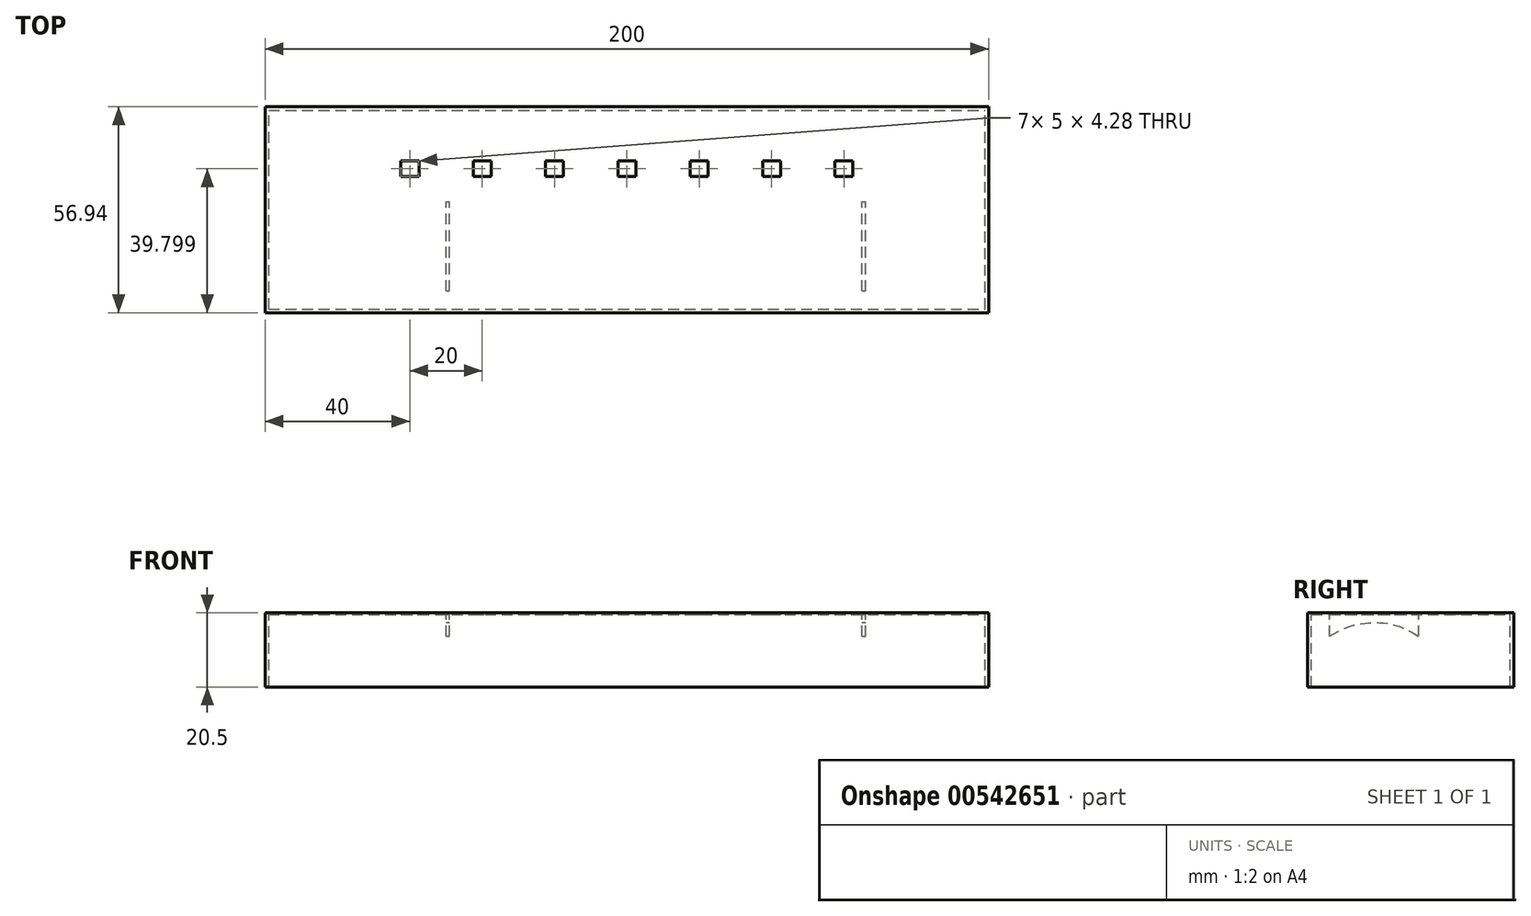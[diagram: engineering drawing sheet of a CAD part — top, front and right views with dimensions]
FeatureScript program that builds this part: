
annotation { "Feature Type Name" : "Feature", "Feature Type Description" : "" }
export const myFeature = defineFeature(function(context is Context, id is Id, definition is map)
    precondition{}
    {
        {
            var Q0;
            Q0=qCreatedBy(makeId("Top.planeOp"),FACE);
            var sketch = newSketch(context, id + "F0", { "sketchPlane" : qUnion([Q0])});
            skLineSegment(sketch, "E0.bottom", {"start": v(100, -28.47) * mm, "end": v(-100, -28.47) * mm});
            skLineSegment(sketch, "E0.top", {"start": v(100, 28.47) * mm, "end": v(-100, 28.47) * mm});
            skLineSegment(sketch, "E0.left", {"start": v(100, -28.47) * mm, "end": v(100, 28.47) * mm});
            skLineSegment(sketch, "E0.right", {"start": v(-100, -28.47) * mm, "end": v(-100, 28.47) * mm});
            skPoint(sketch, "E0.middle", {"position": v(0, 0) * mm});
            skLineSegment(sketch, "E1.bottom", {"start": v(-62.5, 13.47) * mm, "end": v(-57.5, 13.47) * mm});
            skLineSegment(sketch, "E1.top", {"start": v(-62.5, 9.19) * mm, "end": v(-57.5, 9.19) * mm});
            skLineSegment(sketch, "E1.left", {"start": v(-62.5, 13.47) * mm, "end": v(-62.5, 9.19) * mm});
            skLineSegment(sketch, "E1.right", {"start": v(-57.5, 13.47) * mm, "end": v(-57.5, 9.19) * mm});
            skLineSegment(sketch, "E2.1.0.0", {"start": v(-42.5, 13.47) * mm, "end": v(-42.5, 9.19) * mm});
            skLineSegment(sketch, "E2.1.0.1", {"start": v(-42.5, 13.47) * mm, "end": v(-37.5, 13.47) * mm});
            skLineSegment(sketch, "E2.1.0.2", {"start": v(-37.5, 13.47) * mm, "end": v(-37.5, 9.19) * mm});
            skLineSegment(sketch, "E2.1.0.3", {"start": v(-42.5, 9.19) * mm, "end": v(-37.5, 9.19) * mm});
            skLineSegment(sketch, "E2.2.0.0", {"start": v(-22.5, 13.47) * mm, "end": v(-22.5, 9.19) * mm});
            skLineSegment(sketch, "E2.2.0.1", {"start": v(-22.5, 13.47) * mm, "end": v(-17.5, 13.47) * mm});
            skLineSegment(sketch, "E2.2.0.2", {"start": v(-17.5, 13.47) * mm, "end": v(-17.5, 9.19) * mm});
            skLineSegment(sketch, "E2.2.0.3", {"start": v(-22.5, 9.19) * mm, "end": v(-17.5, 9.19) * mm});
            skLineSegment(sketch, "E2.3.0.0", {"start": v(-2.5, 13.47) * mm, "end": v(-2.5, 9.19) * mm});
            skLineSegment(sketch, "E2.3.0.1", {"start": v(-2.5, 13.47) * mm, "end": v(2.5, 13.47) * mm});
            skLineSegment(sketch, "E2.3.0.2", {"start": v(2.5, 13.47) * mm, "end": v(2.5, 9.19) * mm});
            skLineSegment(sketch, "E2.3.0.3", {"start": v(-2.5, 9.19) * mm, "end": v(2.5, 9.19) * mm});
            skLineSegment(sketch, "E2.4.0.0", {"start": v(17.5, 13.47) * mm, "end": v(17.5, 9.19) * mm});
            skLineSegment(sketch, "E2.4.0.1", {"start": v(17.5, 13.47) * mm, "end": v(22.5, 13.47) * mm});
            skLineSegment(sketch, "E2.4.0.2", {"start": v(22.5, 13.47) * mm, "end": v(22.5, 9.19) * mm});
            skLineSegment(sketch, "E2.4.0.3", {"start": v(17.5, 9.19) * mm, "end": v(22.5, 9.19) * mm});
            skLineSegment(sketch, "E2.direction1", {"start": v(-62.5, 9.19) * mm, "end": v(-42.5, 9.19) * mm, "construction": true});
            skLineSegment(sketch, "E3.0.5.0", {"start": v(37.5, 13.47) * mm, "end": v(37.5, 9.19) * mm});
            skLineSegment(sketch, "E3.3.5.0", {"start": v(37.5, 13.47) * mm, "end": v(42.5, 13.47) * mm});
            skLineSegment(sketch, "E3.6.5.0", {"start": v(42.5, 13.47) * mm, "end": v(42.5, 9.19) * mm});
            skLineSegment(sketch, "E3.9.5.0", {"start": v(37.5, 9.19) * mm, "end": v(42.5, 9.19) * mm});
            skLineSegment(sketch, "E3.0.6.0", {"start": v(57.5, 13.47) * mm, "end": v(57.5, 9.19) * mm});
            skLineSegment(sketch, "E3.3.6.0", {"start": v(57.5, 13.47) * mm, "end": v(62.5, 13.47) * mm});
            skLineSegment(sketch, "E3.6.6.0", {"start": v(62.5, 13.47) * mm, "end": v(62.5, 9.19) * mm});
            skLineSegment(sketch, "E3.9.6.0", {"start": v(57.5, 9.19) * mm, "end": v(62.5, 9.19) * mm});
            skSolve(sketch);
        }
        {
            var Q0;
            Q0 = qSketchRegion(id + "F0", true);
            extrude(context, id + "F1", {"entities" : qUnion([Q0]), "endBound" : BoundingType.SYMMETRIC, "depth" : 1 * mm, "offsetDistance" : 25 * mm});
        }
        {
            var Q0;
            Q0 = qSketchRegion(id + "F0", true);
            extrude(context, id + "F2", {"entities" : qUnion([Q0]), "operationType" : NewBodyOperationType.REMOVE, "endBound" : BoundingType.THROUGH_ALL, "oppositeDirection" : true, "depth" : 25 * mm, "offsetDistance" : 25 * mm});
        }
        {
            var Q0;
            Q0=makeQuery(id+"F2.boolean.opBoolean","COPY",FACE,{"derivedFrom":makeQuery(id+"F2.opExtrude","CAP_FACE",FACE,{"disambiguationData":[OSD([sQuery(id+"F0.wireOp",EDGE,"E0.bottom"),sQuery(id+"F0.wireOp",EDGE,"E0.top"),sQuery(id+"F0.wireOp",EDGE,"E0.left"),sQuery(id+"F0.wireOp",EDGE,"E0.right"),sQuery(id+"F0.wireOp",EDGE,"E1.bottom"),sQuery(id+"F0.wireOp",EDGE,"E1.top"),sQuery(id+"F0.wireOp",EDGE,"E1.left"),sQuery(id+"F0.wireOp",EDGE,"E1.right"),sQuery(id+"F0.wireOp",EDGE,"E2.1.0.0"),sQuery(id+"F0.wireOp",EDGE,"E2.1.0.1"),sQuery(id+"F0.wireOp",EDGE,"E2.1.0.2"),sQuery(id+"F0.wireOp",EDGE,"E2.1.0.3"),sQuery(id+"F0.wireOp",EDGE,"E2.2.0.0"),sQuery(id+"F0.wireOp",EDGE,"E2.2.0.1"),sQuery(id+"F0.wireOp",EDGE,"E2.2.0.2"),sQuery(id+"F0.wireOp",EDGE,"E2.2.0.3"),sQuery(id+"F0.wireOp",EDGE,"E2.3.0.0"),sQuery(id+"F0.wireOp",EDGE,"E2.3.0.1"),sQuery(id+"F0.wireOp",EDGE,"E2.3.0.2"),sQuery(id+"F0.wireOp",EDGE,"E2.3.0.3"),sQuery(id+"F0.wireOp",EDGE,"E2.4.0.0"),sQuery(id+"F0.wireOp",EDGE,"E2.4.0.1"),sQuery(id+"F0.wireOp",EDGE,"E2.4.0.2"),sQuery(id+"F0.wireOp",EDGE,"E2.4.0.3"),sQuery(id+"F0.wireOp",EDGE,"E3.0.5.0"),sQuery(id+"F0.wireOp",EDGE,"E3.3.5.0"),sQuery(id+"F0.wireOp",EDGE,"E3.6.5.0"),sQuery(id+"F0.wireOp",EDGE,"E3.9.5.0"),sQuery(id+"F0.wireOp",EDGE,"E3.0.6.0"),sQuery(id+"F0.wireOp",EDGE,"E3.3.6.0"),sQuery(id+"F0.wireOp",EDGE,"E3.6.6.0"),sQuery(id+"F0.wireOp",EDGE,"E3.9.6.0")])],"isStart":true})});
            var sketch = newSketch(context, id + "F3", { "sketchPlane" : qUnion([Q0])});
            skLineSegment(sketch, "E4.bottom", {"start": v(-50, 22.45) * mm, "end": v(-49, 22.45) * mm});
            skLineSegment(sketch, "E4.top", {"start": v(-50, -2.19) * mm, "end": v(-49, -2.19) * mm});
            skLineSegment(sketch, "E4.left", {"start": v(-50, 22.45) * mm, "end": v(-50, -2.19) * mm});
            skLineSegment(sketch, "E4.right", {"start": v(-49, 22.45) * mm, "end": v(-49, -2.19) * mm});
            skLineSegment(sketch, "E5.1.0.0", {"start": v(66, 22.45) * mm, "end": v(66, -2.19) * mm});
            skLineSegment(sketch, "E5.1.0.1", {"start": v(65, 22.45) * mm, "end": v(65, -2.19) * mm});
            skLineSegment(sketch, "E5.1.0.2", {"start": v(65, -2.19) * mm, "end": v(66, -2.19) * mm});
            skLineSegment(sketch, "E5.1.0.3", {"start": v(65, 22.45) * mm, "end": v(66, 22.45) * mm});
            skLineSegment(sketch, "E5.direction1", {"start": v(-49, -2.19) * mm, "end": v(66, -2.19) * mm, "construction": true});
            skSolve(sketch);
        }
        {
            var Q0;
            Q0 = qSketchRegion(id + "F3", true);
            extrude(context, id + "F4", {"entities" : qUnion([Q0]), "operationType" : NewBodyOperationType.ADD, "depth" : 6 * mm, "offsetDistance" : 25 * mm});
        }
        {
            var Q0;
            Q0=makeQuery(id+"F4.opExtrude","SWEPT_FACE",FACE,{"disambiguationData":[OSD([sQuery(id+"F3.wireOp",EDGE,"E4.left")])]});
            var sketch = newSketch(context, id + "F5", { "sketchPlane" : qUnion([Q0])});
            skPoint(sketch, "E6.1.internal.snap0", {"position": v(10.13, 0) * mm});
            skFitSpline(sketch, "E6", {"points": [v(22.45, -6) * mm, v(10.13, -2.2) * mm, v(-2.19, -6) * mm], "startDerivative": vector(-26.18, 17.08) * mm, "endDerivative": vector(-27.42, -17.93) * mm});
            skSolve(sketch);
        }
        {
            var Q0;
            Q0=makeQuery(id+"F5.imprint","IMPRINT",FACE,{"disambiguationData":[TD([[makeQuery(id+"F5.imprint","IMPRINT",EDGE,{"derivedFrom":sQuery(id+"F5.wireOp",EDGE,"E6")}),1.0]])]});
            extrude(context, id + "F6", {"entities" : qUnion([Q0]), "operationType" : NewBodyOperationType.REMOVE, "endBound" : BoundingType.THROUGH_ALL, "oppositeDirection" : true, "depth" : 25 * mm, "offsetDistance" : 25 * mm});
        }
        {
            var Q0;
            Q0=makeQuery(id+"F2.boolean.opBoolean","COPY",FACE,{"derivedFrom":makeQuery(id+"F2.opExtrude","CAP_FACE",FACE,{"disambiguationData":[OSD([sQuery(id+"F0.wireOp",EDGE,"E0.bottom"),sQuery(id+"F0.wireOp",EDGE,"E0.top"),sQuery(id+"F0.wireOp",EDGE,"E0.left"),sQuery(id+"F0.wireOp",EDGE,"E0.right"),sQuery(id+"F0.wireOp",EDGE,"E1.bottom"),sQuery(id+"F0.wireOp",EDGE,"E1.top"),sQuery(id+"F0.wireOp",EDGE,"E1.left"),sQuery(id+"F0.wireOp",EDGE,"E1.right"),sQuery(id+"F0.wireOp",EDGE,"E2.1.0.0"),sQuery(id+"F0.wireOp",EDGE,"E2.1.0.1"),sQuery(id+"F0.wireOp",EDGE,"E2.1.0.2"),sQuery(id+"F0.wireOp",EDGE,"E2.1.0.3"),sQuery(id+"F0.wireOp",EDGE,"E2.2.0.0"),sQuery(id+"F0.wireOp",EDGE,"E2.2.0.1"),sQuery(id+"F0.wireOp",EDGE,"E2.2.0.2"),sQuery(id+"F0.wireOp",EDGE,"E2.2.0.3"),sQuery(id+"F0.wireOp",EDGE,"E2.3.0.0"),sQuery(id+"F0.wireOp",EDGE,"E2.3.0.1"),sQuery(id+"F0.wireOp",EDGE,"E2.3.0.2"),sQuery(id+"F0.wireOp",EDGE,"E2.3.0.3"),sQuery(id+"F0.wireOp",EDGE,"E2.4.0.0"),sQuery(id+"F0.wireOp",EDGE,"E2.4.0.1"),sQuery(id+"F0.wireOp",EDGE,"E2.4.0.2"),sQuery(id+"F0.wireOp",EDGE,"E2.4.0.3"),sQuery(id+"F0.wireOp",EDGE,"E3.0.5.0"),sQuery(id+"F0.wireOp",EDGE,"E3.3.5.0"),sQuery(id+"F0.wireOp",EDGE,"E3.6.5.0"),sQuery(id+"F0.wireOp",EDGE,"E3.9.5.0"),sQuery(id+"F0.wireOp",EDGE,"E3.0.6.0"),sQuery(id+"F0.wireOp",EDGE,"E3.3.6.0"),sQuery(id+"F0.wireOp",EDGE,"E3.6.6.0"),sQuery(id+"F0.wireOp",EDGE,"E3.9.6.0")])],"isStart":true})});
            var sketch = newSketch(context, id + "F7", { "sketchPlane" : qUnion([Q0])});
            skLineSegment(sketch, "E7.bottom", {"start": v(-100, 28.47) * mm, "end": v(-99, 28.47) * mm});
            skLineSegment(sketch, "E7.top", {"start": v(-100, -28.47) * mm, "end": v(-99, -28.47) * mm});
            skLineSegment(sketch, "E7.left", {"start": v(-100, 28.47) * mm, "end": v(-100, -28.47) * mm});
            skLineSegment(sketch, "E7.right", {"start": v(-99, 28.47) * mm, "end": v(-99, -28.47) * mm});
            skSolve(sketch);
        }
        {
            var Q0;
            {var subQ2=sQuery(id+"F7.wireOp",EDGE,"E7.right");Q0=makeQuery(id+"F7.imprint","IMPRINT",FACE,{"disambiguationData":[TD([[makeQuery(id+"F7.imprint","IMPRINT",EDGE,{"derivedFrom":subQ2}),1.0]])]});}
            var sketch = newSketch(context, id + "F8", { "sketchPlane" : qUnion([Q0])});
            skLineSegment(sketch, "E8.bottom", {"start": v(100, 28.47) * mm, "end": v(99, 28.47) * mm});
            skLineSegment(sketch, "E8.top", {"start": v(100, -28.47) * mm, "end": v(99, -28.47) * mm});
            skLineSegment(sketch, "E8.left", {"start": v(100, 28.47) * mm, "end": v(100, -28.47) * mm});
            skLineSegment(sketch, "E8.right", {"start": v(99, 28.47) * mm, "end": v(99, -28.47) * mm});
            skSolve(sketch);
        }
        {
            var Q0;
            Q0 = qSketchRegion(id + "F8", true);
            extrude(context, id + "F9", {"entities" : qUnion([Q0]), "operationType" : NewBodyOperationType.ADD, "depth" : 20 * mm, "offsetDistance" : 25 * mm});
        }
        {
            var Q0;
            Q0 = qSketchRegion(id + "F7", true);
            extrude(context, id + "F10", {"entities" : qUnion([Q0]), "operationType" : NewBodyOperationType.ADD, "depth" : 20 * mm, "offsetDistance" : 25 * mm});
        }
        {
            var Q0;
            Q0=makeQuery(id+"F2.boolean.opBoolean","COPY",FACE,{"derivedFrom":makeQuery(id+"F2.opExtrude","CAP_FACE",FACE,{"disambiguationData":[OSD([sQuery(id+"F0.wireOp",EDGE,"E0.bottom"),sQuery(id+"F0.wireOp",EDGE,"E0.top"),sQuery(id+"F0.wireOp",EDGE,"E0.left"),sQuery(id+"F0.wireOp",EDGE,"E0.right"),sQuery(id+"F0.wireOp",EDGE,"E1.bottom"),sQuery(id+"F0.wireOp",EDGE,"E1.top"),sQuery(id+"F0.wireOp",EDGE,"E1.left"),sQuery(id+"F0.wireOp",EDGE,"E1.right"),sQuery(id+"F0.wireOp",EDGE,"E2.1.0.0"),sQuery(id+"F0.wireOp",EDGE,"E2.1.0.1"),sQuery(id+"F0.wireOp",EDGE,"E2.1.0.2"),sQuery(id+"F0.wireOp",EDGE,"E2.1.0.3"),sQuery(id+"F0.wireOp",EDGE,"E2.2.0.0"),sQuery(id+"F0.wireOp",EDGE,"E2.2.0.1"),sQuery(id+"F0.wireOp",EDGE,"E2.2.0.2"),sQuery(id+"F0.wireOp",EDGE,"E2.2.0.3"),sQuery(id+"F0.wireOp",EDGE,"E2.3.0.0"),sQuery(id+"F0.wireOp",EDGE,"E2.3.0.1"),sQuery(id+"F0.wireOp",EDGE,"E2.3.0.2"),sQuery(id+"F0.wireOp",EDGE,"E2.3.0.3"),sQuery(id+"F0.wireOp",EDGE,"E2.4.0.0"),sQuery(id+"F0.wireOp",EDGE,"E2.4.0.1"),sQuery(id+"F0.wireOp",EDGE,"E2.4.0.2"),sQuery(id+"F0.wireOp",EDGE,"E2.4.0.3"),sQuery(id+"F0.wireOp",EDGE,"E3.0.5.0"),sQuery(id+"F0.wireOp",EDGE,"E3.3.5.0"),sQuery(id+"F0.wireOp",EDGE,"E3.6.5.0"),sQuery(id+"F0.wireOp",EDGE,"E3.9.5.0"),sQuery(id+"F0.wireOp",EDGE,"E3.0.6.0"),sQuery(id+"F0.wireOp",EDGE,"E3.3.6.0"),sQuery(id+"F0.wireOp",EDGE,"E3.6.6.0"),sQuery(id+"F0.wireOp",EDGE,"E3.9.6.0")])],"isStart":true})});
            var sketch = newSketch(context, id + "F11", { "sketchPlane" : qUnion([Q0])});
            skLineSegment(sketch, "E9.bottom", {"start": v(-99, 28.47) * mm, "end": v(99, 28.47) * mm});
            skLineSegment(sketch, "E9.top", {"start": v(-99, 27.47) * mm, "end": v(99, 27.47) * mm});
            skLineSegment(sketch, "E9.left", {"start": v(-99, 28.47) * mm, "end": v(-99, 27.47) * mm});
            skLineSegment(sketch, "E9.right", {"start": v(99, 28.47) * mm, "end": v(99, 27.47) * mm});
            skSolve(sketch);
        }
        {
            var Q0;
            Q0 = qSketchRegion(id + "F11", true);
            extrude(context, id + "F12", {"entities" : qUnion([Q0]), "operationType" : NewBodyOperationType.ADD, "depth" : 20 * mm, "offsetDistance" : 25 * mm});
        }
        {
            var Q0;
            Q0=makeQuery(id+"F2.boolean.opBoolean","COPY",FACE,{"derivedFrom":makeQuery(id+"F2.opExtrude","CAP_FACE",FACE,{"disambiguationData":[OSD([sQuery(id+"F0.wireOp",EDGE,"E0.bottom"),sQuery(id+"F0.wireOp",EDGE,"E0.top"),sQuery(id+"F0.wireOp",EDGE,"E0.left"),sQuery(id+"F0.wireOp",EDGE,"E0.right"),sQuery(id+"F0.wireOp",EDGE,"E1.bottom"),sQuery(id+"F0.wireOp",EDGE,"E1.top"),sQuery(id+"F0.wireOp",EDGE,"E1.left"),sQuery(id+"F0.wireOp",EDGE,"E1.right"),sQuery(id+"F0.wireOp",EDGE,"E2.1.0.0"),sQuery(id+"F0.wireOp",EDGE,"E2.1.0.1"),sQuery(id+"F0.wireOp",EDGE,"E2.1.0.2"),sQuery(id+"F0.wireOp",EDGE,"E2.1.0.3"),sQuery(id+"F0.wireOp",EDGE,"E2.2.0.0"),sQuery(id+"F0.wireOp",EDGE,"E2.2.0.1"),sQuery(id+"F0.wireOp",EDGE,"E2.2.0.2"),sQuery(id+"F0.wireOp",EDGE,"E2.2.0.3"),sQuery(id+"F0.wireOp",EDGE,"E2.3.0.0"),sQuery(id+"F0.wireOp",EDGE,"E2.3.0.1"),sQuery(id+"F0.wireOp",EDGE,"E2.3.0.2"),sQuery(id+"F0.wireOp",EDGE,"E2.3.0.3"),sQuery(id+"F0.wireOp",EDGE,"E2.4.0.0"),sQuery(id+"F0.wireOp",EDGE,"E2.4.0.1"),sQuery(id+"F0.wireOp",EDGE,"E2.4.0.2"),sQuery(id+"F0.wireOp",EDGE,"E2.4.0.3"),sQuery(id+"F0.wireOp",EDGE,"E3.0.5.0"),sQuery(id+"F0.wireOp",EDGE,"E3.3.5.0"),sQuery(id+"F0.wireOp",EDGE,"E3.6.5.0"),sQuery(id+"F0.wireOp",EDGE,"E3.9.5.0"),sQuery(id+"F0.wireOp",EDGE,"E3.0.6.0"),sQuery(id+"F0.wireOp",EDGE,"E3.3.6.0"),sQuery(id+"F0.wireOp",EDGE,"E3.6.6.0"),sQuery(id+"F0.wireOp",EDGE,"E3.9.6.0")])],"isStart":true})});
            var sketch = newSketch(context, id + "F13", { "sketchPlane" : qUnion([Q0])});
            skLineSegment(sketch, "E10.bottom", {"start": v(-99, -28.47) * mm, "end": v(99, -28.47) * mm});
            skLineSegment(sketch, "E10.top", {"start": v(-99, -27.47) * mm, "end": v(99, -27.47) * mm});
            skLineSegment(sketch, "E10.left", {"start": v(-99, -28.47) * mm, "end": v(-99, -27.47) * mm});
            skLineSegment(sketch, "E10.right", {"start": v(99, -28.47) * mm, "end": v(99, -27.47) * mm});
            skSolve(sketch);
        }
        {
            var Q0;
            Q0 = qSketchRegion(id + "F13", true);
            extrude(context, id + "F14", {"entities" : qUnion([Q0]), "operationType" : NewBodyOperationType.ADD, "depth" : 20 * mm, "offsetDistance" : 25 * mm});
        }
    });
